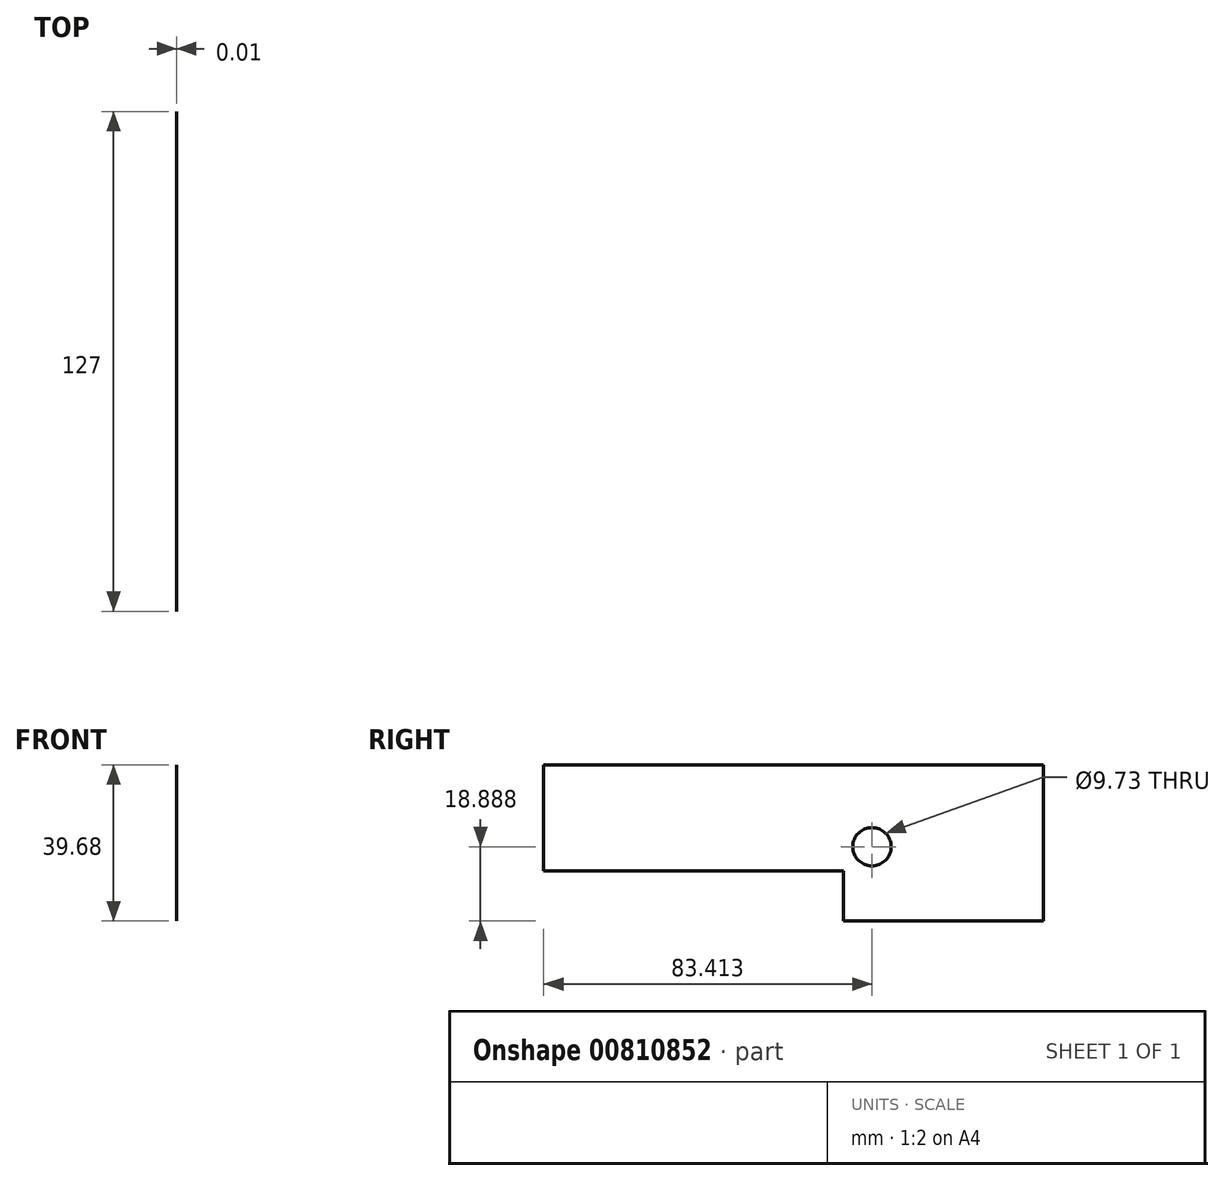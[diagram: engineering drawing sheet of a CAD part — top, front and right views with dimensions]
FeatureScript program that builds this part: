
annotation { "Feature Type Name" : "Feature", "Feature Type Description" : "" }
export const myFeature = defineFeature(function(context is Context, id is Id, definition is map)
    precondition{}
    {
        {
            var Q0;
            Q0=qCreatedBy(makeId("Right.planeOp"),FACE);
            var sketch = newSketch(context, id + "F0", { "sketchPlane" : qUnion([Q0])});
            skLineSegment(sketch, "E0.bottom", {"start": v(-63.5, 7.14) * mm, "end": v(63.5, 7.14) * mm});
            skLineSegment(sketch, "E0.top", {"start": v(-63.5, -7.14) * mm, "end": v(63.5, -7.14) * mm});
            skLineSegment(sketch, "E0.left", {"start": v(-63.5, 7.14) * mm, "end": v(-63.5, -7.14) * mm});
            skLineSegment(sketch, "E0.right", {"start": v(63.5, 7.14) * mm, "end": v(63.5, -7.14) * mm});
            skPoint(sketch, "E0.middle", {"position": v(0, 0) * mm});
            skLineSegment(sketch, "E1.bottom", {"start": v(63.5, -7.14) * mm, "end": v(12.7, -7.14) * mm});
            skLineSegment(sketch, "E1.top", {"start": v(63.5, -32.54) * mm, "end": v(12.7, -32.54) * mm});
            skLineSegment(sketch, "E1.left", {"start": v(63.5, -7.14) * mm, "end": v(63.5, -32.54) * mm});
            skLineSegment(sketch, "E1.right", {"start": v(12.7, -7.14) * mm, "end": v(12.7, -32.54) * mm});
            skCircle(sketch, "E2", {"center": v(19.91, -13.65) * mm, "radius": 4.87 * mm});
            skLineSegment(sketch, "E3.bottom", {"start": v(12.7, -19.84) * mm, "end": v(-63.5, -19.84) * mm});
            skLineSegment(sketch, "E3.top", {"start": v(12.7, -7.14) * mm, "end": v(-63.5, -7.14) * mm});
            skLineSegment(sketch, "E3.left", {"start": v(12.7, -19.84) * mm, "end": v(12.7, -7.14) * mm});
            skLineSegment(sketch, "E3.right", {"start": v(-63.5, -19.84) * mm, "end": v(-63.5, -7.14) * mm});
            skLineSegment(sketch, "E4.bottom", {"start": v(12.7, -19.84) * mm, "end": v(12.7, -19.84) * mm});
            skLineSegment(sketch, "E4.top", {"start": v(12.7, -32.54) * mm, "end": v(12.7, -32.54) * mm});
            skLineSegment(sketch, "E4.left", {"start": v(12.7, -19.84) * mm, "end": v(12.7, -32.54) * mm});
            skLineSegment(sketch, "E4.right", {"start": v(12.7, -19.84) * mm, "end": v(12.7, -32.54) * mm});
            skSolve(sketch);
        }
        {
            var Q0;
            Q0=makeQuery(id+"F0.imprint","IMPRINT",FACE,{"disambiguationData":[TD([[makeQuery(id+"F0.imprint","IMPRINT",EDGE,{"derivedFrom":sQuery(id+"F0.wireOp",EDGE,"E0.bottom")}),-1.0]])]});
            var Q1;
            {var subQ1=sQuery(id+"F0.wireOp",EDGE,"E1.top");Q1=makeQuery(id+"F0.imprint","IMPRINT",FACE,{"disambiguationData":[TD([[makeQuery(id+"F0.imprint","IMPRINT",EDGE,{"derivedFrom":subQ1}),-1.0]])]});}
            var Q2;
            {var subQ4=sQuery(id+"F0.wireOp",EDGE,"E3.bottom");Q2=makeQuery(id+"F0.imprint","IMPRINT",FACE,{"disambiguationData":[TD([[makeQuery(id+"F0.imprint","IMPRINT",EDGE,{"derivedFrom":subQ4}),-1.0]])]});}
            var Q3;
            {var subQ4=sQuery(id+"F0.wireOp",EDGE,"E3.bottom");Q3=makeQuery(id+"F0.imprint","IMPRINT",FACE,{"disambiguationData":[TD([[makeQuery(id+"F0.imprint","IMPRINT",EDGE,{"derivedFrom":subQ4}),-1.0]])]});}
            var Q4;
            Q4=makeQuery(id+"F0.imprint","IMPRINT",FACE,{"disambiguationData":[TD([[makeQuery(id+"F0.imprint","IMPRINT",EDGE,{"derivedFrom":sQuery(id+"F0.wireOp",EDGE,"1ntXL32u-kZwH-qWFd-F0QC-1M4kifk4ORWq.bottom")}),1.0]])]});
            extrude(context, id + "F1", {"entities" : qUnion([Q0, Q1, Q2, Q3, Q4]), "oppositeDirection" : true, "depth" : 1 / 101.6 * mm, "offsetDistance" : 25.4 * mm});
        }
    });
